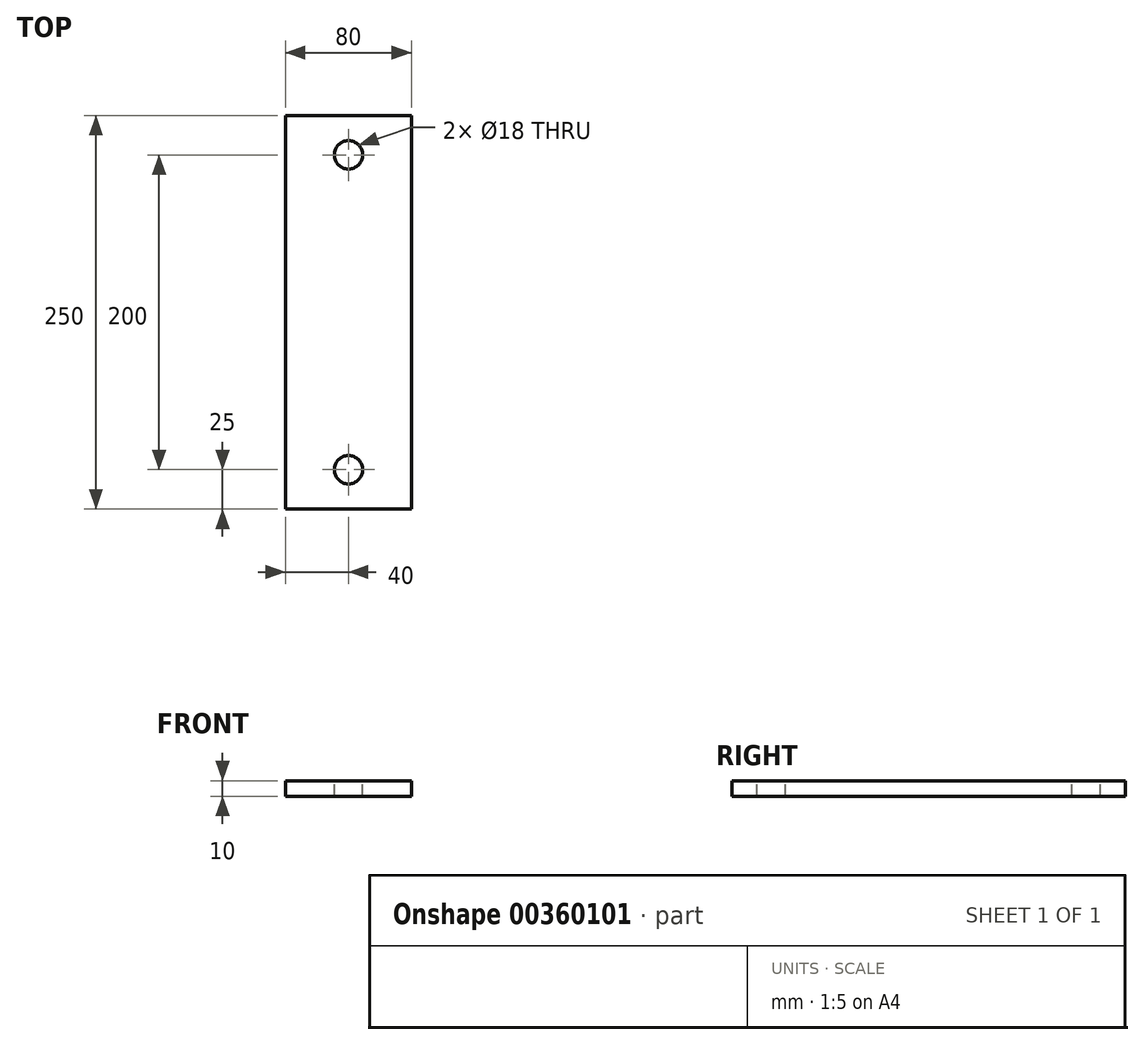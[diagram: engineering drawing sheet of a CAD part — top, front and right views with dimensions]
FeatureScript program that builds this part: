
annotation { "Feature Type Name" : "Feature", "Feature Type Description" : "" }
export const myFeature = defineFeature(function(context is Context, id is Id, definition is map)
    precondition{}
    {
        {
            var Q0;
            Q0=qCreatedBy(makeId("Top.planeOp"),FACE);
            var sketch = newSketch(context, id + "F0", { "sketchPlane" : qUnion([Q0])});
            skLineSegment(sketch, "E0.bottom", {"start": v(40, -125) * mm, "end": v(-40, -125) * mm});
            skLineSegment(sketch, "E0.top", {"start": v(40, 125) * mm, "end": v(-40, 125) * mm});
            skLineSegment(sketch, "E0.left", {"start": v(40, -125) * mm, "end": v(40, 125) * mm});
            skLineSegment(sketch, "E0.right", {"start": v(-40, -125) * mm, "end": v(-40, 125) * mm});
            skPoint(sketch, "E0.middle", {"position": v(0, 0) * mm});
            skSolve(sketch);
        }
        {
            var Q0;
            Q0 = qSketchRegion(id + "F0", true);
            extrude(context, id + "F1", {"entities" : qUnion([Q0]), "depth" : 10 * mm});
        }
        {
            var Q0;
            Q0=makeQuery(id+"F1.opExtrude","CAP_FACE",FACE,{"disambiguationData":[OSD([sQuery(id+"F0.wireOp",EDGE,"E0.bottom"),sQuery(id+"F0.wireOp",EDGE,"E0.top"),sQuery(id+"F0.wireOp",EDGE,"E0.left"),sQuery(id+"F0.wireOp",EDGE,"E0.right")])],"isStart":false});
            var sketch = newSketch(context, id + "F2", { "sketchPlane" : qUnion([Q0])});
            skLineSegment(sketch, "E1", {"start": v(0, 125) * mm, "end": v(0, 100) * mm});
            skPoint(sketch, "E1.endSnap0", {"position": v(0, 125) * mm});
            skLineSegment(sketch, "E2", {"start": v(0, -125) * mm, "end": v(0, -100) * mm});
            skPoint(sketch, "E2.endSnap0", {"position": v(0, -125) * mm});
            skSolve(sketch);
        }
        {
            var Q0;
            Q0=sQuery(id+"F2.wireOp",VERTEX,"E1.end");
            var Q1;
            Q1=sQuery(id+"F2.wireOp",VERTEX,"E2.end");
            var Q2;
            Q2=makeQuery(id+"F1.opExtrude","SWEPT_BODY",BODY,{"disambiguationData":[OSD([sQuery(id+"F0.wireOp",EDGE,"E0.bottom"),sQuery(id+"F0.wireOp",EDGE,"E0.top"),sQuery(id+"F0.wireOp",EDGE,"E0.left"),sQuery(id+"F0.wireOp",EDGE,"E0.right")])]});
            hole(context, id + "F3", {"style" : HoleStyle.SIMPLE, "endStyle" : HoleEndStyle.THROUGH, "holeDiameter" : 18 * mm, "isTappedThrough" : true, "tappedDepth" : 12 * mm, "tapClearance" : 3, "locations" : qUnion([Q0, Q1]), "scope" : qUnion([Q2])});
        }
    });
